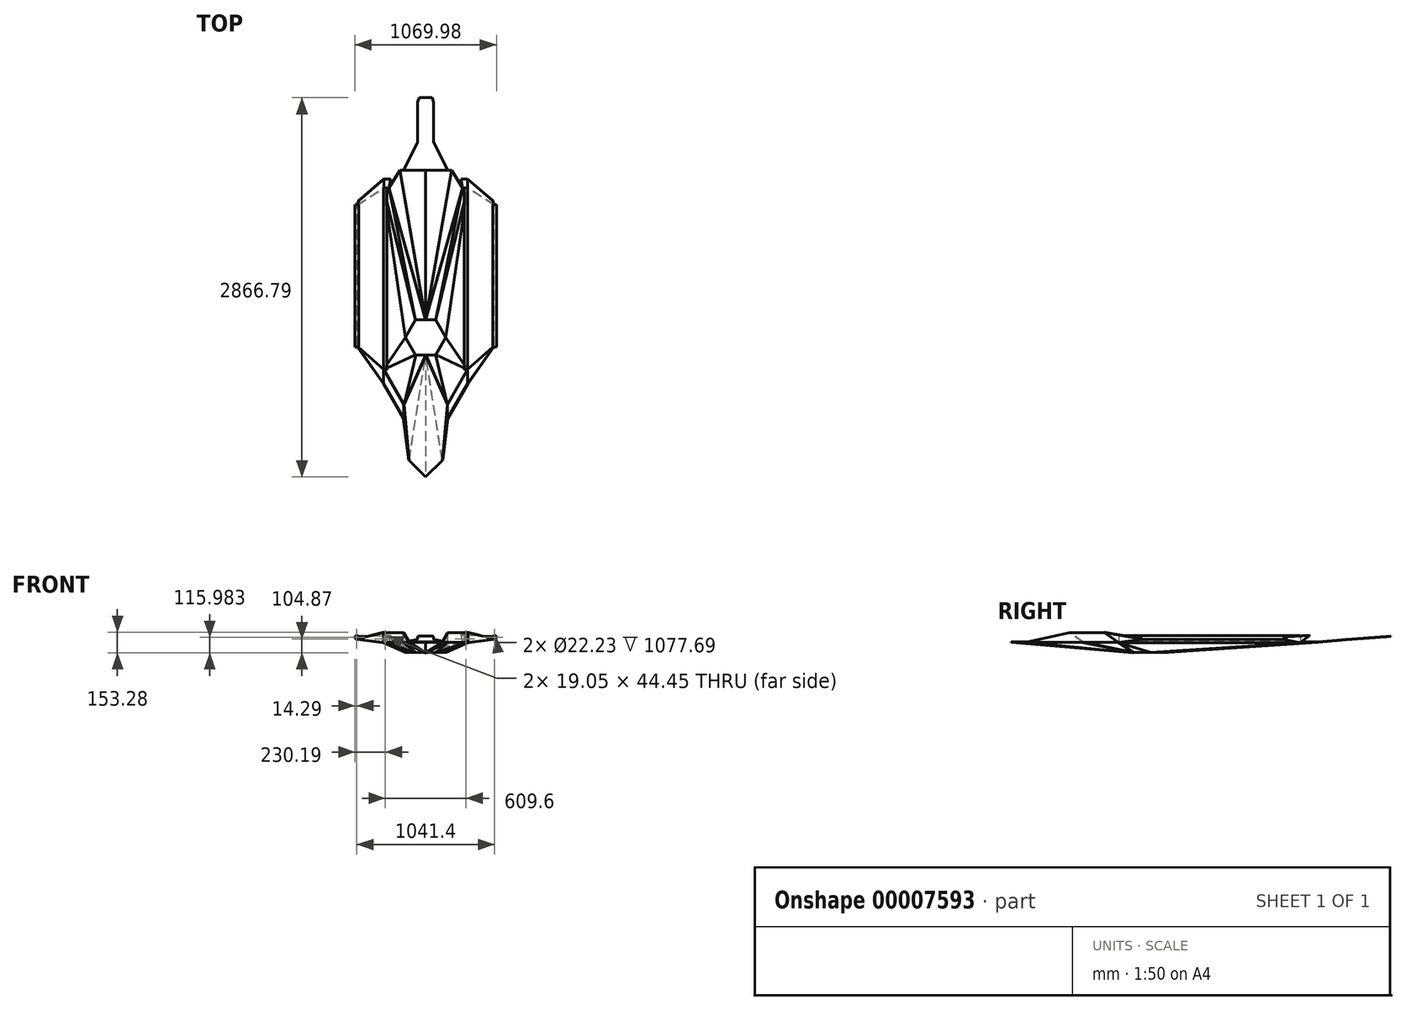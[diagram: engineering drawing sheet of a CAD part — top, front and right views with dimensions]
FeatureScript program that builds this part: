
annotation { "Feature Type Name" : "Feature", "Feature Type Description" : "" }
export const myFeature = defineFeature(function(context is Context, id is Id, definition is map)
    precondition{}
    {
        {
            var Q0;
            Q0=qCreatedBy(makeId("Top.planeOp"),FACE);
            var sketch = newSketch(context, id + "F0", { "sketchPlane" : qUnion([Q0])});
            skLineSegment(sketch, "E0.bottom", {"start": v(-317.5, -685.8) * mm, "end": v(317.5, -685.8) * mm});
            skLineSegment(sketch, "E0.top", {"start": v(-317.5, 685.8) * mm, "end": v(317.5, 685.8) * mm});
            skLineSegment(sketch, "E0.left", {"start": v(-317.5, -685.8) * mm, "end": v(-317.5, 685.8) * mm});
            skLineSegment(sketch, "E0.right", {"start": v(317.5, -685.8) * mm, "end": v(317.5, 685.8) * mm});
            skPoint(sketch, "E0.middle", {"position": v(0, 0) * mm});
            skLineSegment(sketch, "E1", {"start": v(0, -1498.6) * mm, "end": v(0, 1371.6) * mm, "construction": true});
            skLineSegment(sketch, "E2.0", {"start": v(-520.7, -508) * mm, "end": v(-520.7, 558.8) * mm});
            skLineSegment(sketch, "E3.0", {"start": v(520.7, -508) * mm, "end": v(520.7, 558.8) * mm});
            skLineSegment(sketch, "E4", {"start": v(317.5, -685.8) * mm, "end": v(520.7, -508) * mm});
            skLineSegment(sketch, "E5", {"start": v(520.7, 558.8) * mm, "end": v(317.5, 685.8) * mm});
            skLineSegment(sketch, "E6.MirrorCS", {"start": v(-520.7, 558.8) * mm, "end": v(-317.5, 685.8) * mm});
            skLineSegment(sketch, "E7.MirrorCS", {"start": v(-317.5, -685.8) * mm, "end": v(-520.7, -508) * mm});
            skLineSegment(sketch, "E8", {"start": v(278.86, 685.8) * mm, "end": v(195.2, 819.67) * mm});
            skLineSegment(sketch, "E9", {"start": v(195.2, 819.67) * mm, "end": v(167.22, 819.67) * mm});
            skLineSegment(sketch, "E10.MirrorCS", {"start": v(-195.2, 819.67) * mm, "end": v(-167.22, 819.67) * mm});
            skLineSegment(sketch, "E11.MirrorCS", {"start": v(-278.86, 685.8) * mm, "end": v(-195.2, 819.67) * mm});
            skLineSegment(sketch, "E12", {"start": v(317.5, -685.8) * mm, "end": v(164.9, -952) * mm});
            skLineSegment(sketch, "E13", {"start": v(164.9, -952) * mm, "end": v(125.97, -1373.7) * mm});
            skLineSegment(sketch, "E14", {"start": v(125.97, -1373.7) * mm, "end": v(0, -1498.6) * mm});
            skLineSegment(sketch, "E15.MirrorCS", {"start": v(-164.9, -952) * mm, "end": v(-125.97, -1373.7) * mm});
            skLineSegment(sketch, "E16.MirrorCS", {"start": v(-317.5, -685.8) * mm, "end": v(-164.9, -952) * mm});
            skLineSegment(sketch, "E17.MirrorCS", {"start": v(-125.97, -1373.7) * mm, "end": v(0, -1498.6) * mm});
            skLineSegment(sketch, "E18", {"start": v(167.22, 819.67) * mm, "end": v(60.58, 1033.46) * mm});
            skLineSegment(sketch, "E19", {"start": v(60.58, 1033.46) * mm, "end": v(60.58, 1338.26) * mm});
            skLineSegment(sketch, "E20", {"start": v(60.58, 1338.26) * mm, "end": v(50.3, 1371.6) * mm});
            skLineSegment(sketch, "E21", {"start": v(50.3, 1371.6) * mm, "end": v(0, 1371.6) * mm});
            skLineSegment(sketch, "E22.MirrorCS", {"start": v(-50.3, 1371.6) * mm, "end": v(0, 1371.6) * mm});
            skLineSegment(sketch, "E23.MirrorCS", {"start": v(-60.58, 1338.26) * mm, "end": v(-50.3, 1371.6) * mm});
            skLineSegment(sketch, "E24.MirrorCS", {"start": v(-60.58, 1033.46) * mm, "end": v(-60.58, 1338.26) * mm});
            skLineSegment(sketch, "E25.MirrorCS", {"start": v(-167.22, 819.67) * mm, "end": v(-60.58, 1033.46) * mm});
            skPoint(sketch, "E26.orphan", {"position": v(0, 819.67) * mm});
            skSolve(sketch);
        }
        {
            var Q0;
            Q0=qCreatedBy(makeId("Top.planeOp"),FACE);
            cPlane(context, id + "F1", {"entities" : qUnion([Q0]), "cplaneType" : CPlaneType.OFFSET, "offset" : 76.2 * mm, "oppositeDirection" : true, "width" : 152.4 * mm, "height" : 152.4 * mm});
        }
        {
            var Q0;
            Q0=qCreatedBy(id+"F1.planeOp",FACE);
            var sketch = newSketch(context, id + "F2", { "sketchPlane" : qUnion([Q0])});
            skCircle(sketch, "E27.cCircle", {"center": v(0, -443.6) * mm, "radius": 131.98 * mm, "construction": true});
            skLineSegment(sketch, "E27.0", {"start": v(76.2, -575.58) * mm, "end": v(-76.2, -575.58) * mm});
            skLineSegment(sketch, "E27.1", {"start": v(-76.2, -575.58) * mm, "end": v(-152.4, -443.6) * mm});
            skLineSegment(sketch, "E27.2", {"start": v(-152.4, -443.6) * mm, "end": v(-76.2, -311.61) * mm});
            skLineSegment(sketch, "E27.3", {"start": v(-76.2, -311.61) * mm, "end": v(76.2, -311.61) * mm});
            skLineSegment(sketch, "E27.4", {"start": v(76.2, -311.61) * mm, "end": v(152.4, -443.6) * mm});
            skLineSegment(sketch, "E27.5", {"start": v(152.4, -443.6) * mm, "end": v(76.2, -575.58) * mm});
            skPoint(sketch, "E27.0.midPoint", {"position": v(0, -575.58) * mm});
            skPoint(sketch, "E28", {"position": v(0, -311.61) * mm});
            skSolve(sketch);
        }
        {
            var Q0;
            Q0 = qSketchRegion(id + "F2", true);
            extrude(context, id + "F3", {"entities" : qUnion([Q0]), "depth" : 3.33 * mm});
        }
        {
            var Q0;
            Q0=makeQuery(id+"F3.opExtrude","CAP_VERTEX",VERTEX,{"disambiguationData":[OSD([sQuery(id+"F2.wireOp",EDGE,"E27.1"),sQuery(id+"F2.wireOp",EDGE,"E27.2")])],"isStart":false});
            var Q1;
            Q1=makeQuery(id+"F3.opExtrude","CAP_VERTEX",VERTEX,{"disambiguationData":[OSD([sQuery(id+"F2.wireOp",EDGE,"E27.2"),sQuery(id+"F2.wireOp",EDGE,"E27.3")])],"isStart":false});
            var Q2;
            Q2=sQuery(id+"F0.wireOp",VERTEX,"E0.left.end");
            cPlane(context, id + "F4", {"entities" : qUnion([Q0, Q1, Q2]), "cplaneType" : CPlaneType.THREE_POINT, "offset" : 152.4 * mm, "width" : 152.4 * mm, "height" : 152.4 * mm});
        }
        {
            var Q0;
            Q0=qCreatedBy(id+"F4.planeOp",FACE);
            var sketch = newSketch(context, id + "F5", { "sketchPlane" : qUnion([Q0])});
            skPoint(sketch, "E29.0", {"position": v(-147.37, 446.76) * mm});
            skPoint(sketch, "E29.1", {"position": v(-70.87, 314.95) * mm});
            skPoint(sketch, "E29.2", {"position": v(-313.12, -684.9) * mm});
            skLineSegment(sketch, "E30", {"start": v(-313.12, -684.9) * mm, "end": v(-70.87, 314.95) * mm});
            skLineSegment(sketch, "E31", {"start": v(-147.37, 446.76) * mm, "end": v(-313.12, -684.9) * mm});
            skLineSegment(sketch, "E32", {"start": v(-147.37, 446.76) * mm, "end": v(-70.87, 314.95) * mm});
            skSolve(sketch);
        }
        {
            var Q0;
            Q0 = qSketchRegion(id + "F5", true);
            extrude(context, id + "F6", {"entities" : qUnion([Q0]), "depth" : 3.33 * mm});
        }
        {
            var Q0;
            Q0=qCreatedBy(makeId("Top.planeOp"),FACE);
            var sketch = newSketch(context, id + "F7", { "sketchPlane" : qUnion([Q0])});
            skPoint(sketch, "E33.0", {"position": v(317.5, 685.8) * mm});
            skPoint(sketch, "E33.1", {"position": v(317.5, -685.8) * mm});
            skLineSegment(sketch, "E34.bottom", {"start": v(317.5, -685.8) * mm, "end": v(292.1, -685.8) * mm});
            skLineSegment(sketch, "E34.top", {"start": v(317.5, 685.8) * mm, "end": v(292.1, 685.8) * mm});
            skLineSegment(sketch, "E34.left", {"start": v(317.5, -685.8) * mm, "end": v(317.5, 685.8) * mm});
            skLineSegment(sketch, "E34.right", {"start": v(292.1, -685.8) * mm, "end": v(292.1, 685.8) * mm});
            skSolve(sketch);
        }
        {
            var Q0;
            Q0=sQuery(id+"F7.wireOp",EDGE,"E34.bottom");
            cPlane(context, id + "F8", {"entities" : qUnion([Q0]), "cplaneType" : CPlaneType.LINE_ANGLE, "offset" : 152.4 * mm, "angle" : 0 * degree, "width" : 152.4 * mm, "height" : 152.4 * mm});
        }
        {
            var Q0;
            Q0=qCreatedBy(id+"F8.planeOp",FACE);
            var sketch = newSketch(context, id + "F9", { "sketchPlane" : qUnion([Q0])});
            skLineSegment(sketch, "E35.bottom", {"start": v(295.28, 50.8) * mm, "end": v(314.33, 50.8) * mm});
            skLineSegment(sketch, "E35.top", {"start": v(295.28, 0) * mm, "end": v(314.33, 0) * mm});
            skLineSegment(sketch, "E35.left", {"start": v(292.1, 47.62) * mm, "end": v(292.1, 3.18) * mm});
            skLineSegment(sketch, "E35.right", {"start": v(317.5, 47.62) * mm, "end": v(317.5, 3.18) * mm});
            skPoint(sketch, "E36.visualSharp", {"position": v(317.5, 0) * mm});
            skArc(sketch, "E36.filletArc", {"start": v(314.33, 0) * mm, "mid": v(316.57, 0.93) * mm, "end": v(317.5, 3.18) * mm});
            skPoint(sketch, "E37.visualSharp", {"position": v(292.1, 0) * mm});
            skArc(sketch, "E37.filletArc", {"start": v(292.1, 3.18) * mm, "mid": v(293.03, 0.93) * mm, "end": v(295.28, 0) * mm});
            skPoint(sketch, "E38.visualSharp", {"position": v(292.1, 50.8) * mm});
            skArc(sketch, "E38.filletArc", {"start": v(295.28, 50.8) * mm, "mid": v(293.03, 49.87) * mm, "end": v(292.1, 47.62) * mm});
            skPoint(sketch, "E39.visualSharp", {"position": v(317.5, 50.8) * mm});
            skArc(sketch, "E39.filletArc", {"start": v(317.5, 47.62) * mm, "mid": v(316.57, 49.87) * mm, "end": v(314.33, 50.8) * mm});
            skLineSegment(sketch, "E40.0", {"start": v(295.28, 47.62) * mm, "end": v(314.33, 47.62) * mm});
            skLineSegment(sketch, "E40.1", {"start": v(295.28, 47.62) * mm, "end": v(295.28, 3.17) * mm});
            skLineSegment(sketch, "E40.2", {"start": v(295.28, 3.17) * mm, "end": v(314.33, 3.17) * mm});
            skLineSegment(sketch, "E40.3", {"start": v(314.33, 47.62) * mm, "end": v(314.33, 3.17) * mm});
            skSolve(sketch);
        }
        {
            var Q0;
            Q0 = qSketchRegion(id + "F9", true);
            extrude(context, id + "F10", {"entities" : qUnion([Q0]), "oppositeDirection" : true, "depth" : 1371.6 * mm});
        }
        {
            var Q0;
            Q0=makeQuery(id+"F10.opExtrude","SWEPT_BODY",BODY,{"disambiguationData":[OSD([sQuery(id+"F9.wireOp",EDGE,"E35.bottom"),sQuery(id+"F9.wireOp",EDGE,"E35.top"),sQuery(id+"F9.wireOp",EDGE,"E35.left"),sQuery(id+"F9.wireOp",EDGE,"E35.right"),sQuery(id+"F9.wireOp",EDGE,"E36.filletArc"),sQuery(id+"F9.wireOp",EDGE,"E37.filletArc"),sQuery(id+"F9.wireOp",EDGE,"E38.filletArc"),sQuery(id+"F9.wireOp",EDGE,"E39.filletArc"),sQuery(id+"F9.wireOp",EDGE,"E40.0"),sQuery(id+"F9.wireOp",EDGE,"E40.1"),sQuery(id+"F9.wireOp",EDGE,"E40.2"),sQuery(id+"F9.wireOp",EDGE,"E40.3")])]});
            var Q1;
            Q1=qCreatedBy(makeId("Right.planeOp"),FACE);
            mirror(context, id + "F11", {"entities" : qUnion([Q0]), "mirrorPlane" : qUnion([Q1])});
        }
        {
            var Q0;
            Q0=makeQuery(id+"F6.opExtrude","SWEPT_BODY",BODY,{"disambiguationData":[OSD([sQuery(id+"F5.wireOp",EDGE,"E30"),sQuery(id+"F5.wireOp",EDGE,"E31"),sQuery(id+"F5.wireOp",EDGE,"E32")])]});
            var Q1;
            Q1=qCreatedBy(makeId("Right.planeOp"),FACE);
            mirror(context, id + "F12", {"entities" : qUnion([Q0]), "mirrorPlane" : qUnion([Q1])});
        }
        {
            var Q0;
            Q0=makeQuery(id+"F12.opPattern","COPY",VERTEX,{"derivedFrom":makeQuery(id+"F6.opExtrude","CAP_VERTEX",VERTEX,{"disambiguationData":[OSD([sQuery(id+"F5.wireOp",EDGE,"E31"),sQuery(id+"F5.wireOp",EDGE,"E32")])],"isStart":true}),"instanceName":"1"});
            var Q1;
            Q1=makeQuery(id+"F3.opExtrude","CAP_VERTEX",VERTEX,{"disambiguationData":[OSD([sQuery(id+"F2.wireOp",EDGE,"E27.0"),sQuery(id+"F2.wireOp",EDGE,"E27.5")])],"isStart":false});
            var Q2;
            Q2=sQuery(id+"F7.wireOp",VERTEX,"E33.1");
            cPlane(context, id + "F13", {"entities" : qUnion([Q0, Q1, Q2]), "cplaneType" : CPlaneType.THREE_POINT, "offset" : 152.4 * mm, "width" : 152.4 * mm, "height" : 152.4 * mm});
        }
        {
            var Q0;
            Q0=qCreatedBy(id+"F13.planeOp",FACE);
            var sketch = newSketch(context, id + "F14", { "sketchPlane" : qUnion([Q0])});
            skPoint(sketch, "E41.0", {"position": v(38.64, 559.76) * mm});
            skPoint(sketch, "E41.1", {"position": v(116.94, 429.02) * mm});
            skPoint(sketch, "E41.2", {"position": v(287.37, 679.36) * mm});
            skLineSegment(sketch, "E42", {"start": v(116.94, 429.02) * mm, "end": v(287.37, 679.36) * mm});
            skLineSegment(sketch, "E43", {"start": v(116.94, 429.02) * mm, "end": v(38.64, 559.76) * mm});
            skLineSegment(sketch, "E44", {"start": v(38.64, 559.76) * mm, "end": v(287.37, 679.36) * mm});
            skSolve(sketch);
        }
        {
            var Q0;
            Q0 = qSketchRegion(id + "F14", true);
            extrude(context, id + "F15", {"entities" : qUnion([Q0]), "depth" : 3.33 * mm});
        }
        {
            var Q0;
            Q0=makeQuery(id+"F15.opExtrude","SWEPT_BODY",BODY,{"disambiguationData":[OSD([sQuery(id+"F14.wireOp",EDGE,"E42"),sQuery(id+"F14.wireOp",EDGE,"E43"),sQuery(id+"F14.wireOp",EDGE,"E44")])]});
            var Q1;
            Q1=qCreatedBy(makeId("Right.planeOp"),FACE);
            mirror(context, id + "F16", {"operationType" : NewBodyOperationType.ADD, "entities" : qUnion([Q0]), "mirrorPlane" : qUnion([Q1])});
        }
        {
            var Q0;
            Q0=sQuery(id+"F5.wireOp",VERTEX,"E29.0");
            var Q1;
            Q1=makeQuery(id+"F16.opPattern","COPY",VERTEX,{"derivedFrom":makeQuery(id+"F15.opExtrude","CAP_VERTEX",VERTEX,{"disambiguationData":[OSD([sQuery(id+"F14.wireOp",EDGE,"E42"),sQuery(id+"F14.wireOp",EDGE,"E44")])],"isStart":true}),"instanceName":"1"});
            var Q2;
            Q2=sQuery(id+"F5.wireOp",VERTEX,"E29.2");
            cPlane(context, id + "F17", {"entities" : qUnion([Q0, Q1, Q2]), "cplaneType" : CPlaneType.THREE_POINT, "offset" : 152.4 * mm, "width" : 152.4 * mm, "height" : 152.4 * mm});
        }
        {
            var Q0;
            Q0=qCreatedBy(id+"F17.planeOp",FACE);
            var sketch = newSketch(context, id + "F18", { "sketchPlane" : qUnion([Q0])});
            skPoint(sketch, "E45.0", {"position": v(-110, -443.6) * mm});
            skPoint(sketch, "E45.1", {"position": v(-290.46, -685.8) * mm});
            skPoint(sketch, "E45.2", {"position": v(-290.46, 685.8) * mm});
            skLineSegment(sketch, "E46", {"start": v(-290.46, -685.8) * mm, "end": v(-110, -443.6) * mm});
            skLineSegment(sketch, "E47", {"start": v(-290.46, 685.8) * mm, "end": v(-290.46, -685.8) * mm});
            skLineSegment(sketch, "E48", {"start": v(-110, -443.6) * mm, "end": v(-290.46, 685.8) * mm});
            skSolve(sketch);
        }
        {
            var Q0;
            Q0 = qSketchRegion(id + "F18", true);
            extrude(context, id + "F19", {"entities" : qUnion([Q0]), "oppositeDirection" : true, "depth" : 3.33 * mm});
        }
        {
            var Q0;
            Q0=makeQuery(id+"F19.opExtrude","SWEPT_BODY",BODY,{"disambiguationData":[OSD([sQuery(id+"F18.wireOp",EDGE,"E46"),sQuery(id+"F18.wireOp",EDGE,"E47"),sQuery(id+"F18.wireOp",EDGE,"E48")])]});
            var Q1;
            Q1=qCreatedBy(makeId("Right.planeOp"),FACE);
            mirror(context, id + "F20", {"operationType" : NewBodyOperationType.ADD, "entities" : qUnion([Q0]), "mirrorPlane" : qUnion([Q1])});
        }
        {
            var Q0;
            Q0=sQuery(id+"F2.wireOp",VERTEX,"E27.0.midPoint");
            var Q1;
            Q1=sQuery(id+"F14.wireOp",VERTEX,"E41.0");
            var Q2;
            Q2=sQuery(id+"F0.wireOp",VERTEX,"E13.start");
            cPlane(context, id + "F21", {"entities" : qUnion([Q0, Q1, Q2]), "cplaneType" : CPlaneType.THREE_POINT, "offset" : 152.4 * mm, "width" : 152.4 * mm, "height" : 152.4 * mm});
        }
        {
            var Q0;
            Q0=qCreatedBy(id+"F21.planeOp",FACE);
            var sketch = newSketch(context, id + "F22", { "sketchPlane" : qUnion([Q0])});
            skPoint(sketch, "E49.0", {"position": v(-7.4, -552.28) * mm});
            skPoint(sketch, "E49.1", {"position": v(68.74, -552.28) * mm});
            skPoint(sketch, "E49.2", {"position": v(157.64, -936.27) * mm});
            skLineSegment(sketch, "E50", {"start": v(-7.4, -552.28) * mm, "end": v(68.74, -552.28) * mm});
            skLineSegment(sketch, "E51", {"start": v(-7.4, -552.28) * mm, "end": v(157.64, -936.27) * mm});
            skLineSegment(sketch, "E52", {"start": v(68.74, -552.28) * mm, "end": v(157.64, -936.27) * mm});
            skSolve(sketch);
        }
        {
            var Q0;
            Q0 = qSketchRegion(id + "F22", true);
            extrude(context, id + "F23", {"entities" : qUnion([Q0]), "oppositeDirection" : true, "depth" : 3.33 * mm});
        }
        {
            var Q0;
            Q0=sQuery(id+"F2.wireOp",VERTEX,"E27.5.end");
            var Q1;
            Q1=sQuery(id+"F0.wireOp",VERTEX,"E13.start");
            var Q2;
            Q2=sQuery(id+"F14.wireOp",VERTEX,"E41.2");
            cPlane(context, id + "F24", {"entities" : qUnion([Q0, Q1, Q2]), "cplaneType" : CPlaneType.THREE_POINT, "offset" : 152.4 * mm, "width" : 152.4 * mm, "height" : 152.4 * mm});
        }
        {
            var Q0;
            Q0=qCreatedBy(id+"F24.planeOp",FACE);
            var sketch = newSketch(context, id + "F25", { "sketchPlane" : qUnion([Q0])});
            skPoint(sketch, "E53.0", {"position": v(127.55, 942.35) * mm});
            skPoint(sketch, "E53.1", {"position": v(284.77, 678.85) * mm});
            skLineSegment(sketch, "E54", {"start": v(36.17, 558.92) * mm, "end": v(127.55, 942.35) * mm});
            skLineSegment(sketch, "E55", {"start": v(284.77, 678.85) * mm, "end": v(127.55, 942.35) * mm});
            skLineSegment(sketch, "E56", {"start": v(36.17, 558.92) * mm, "end": v(284.77, 678.85) * mm});
            skPoint(sketch, "E57.0", {"position": v(36.17, 558.92) * mm});
            skSolve(sketch);
        }
        {
            var Q0;
            Q0 = qSketchRegion(id + "F25", true);
            extrude(context, id + "F26", {"entities" : qUnion([Q0]), "oppositeDirection" : true, "depth" : 3.33 * mm});
        }
        {
            var Q0;
            Q0=makeQuery(id+"F26.opExtrude","SWEPT_BODY",BODY,{"disambiguationData":[OSD([sQuery(id+"F25.wireOp",EDGE,"E54"),sQuery(id+"F25.wireOp",EDGE,"E55"),sQuery(id+"F25.wireOp",EDGE,"E56")])]});
            var Q1;
            Q1=makeQuery(id+"F23.opExtrude","SWEPT_BODY",BODY,{"disambiguationData":[OSD([sQuery(id+"F22.wireOp",EDGE,"E50"),sQuery(id+"F22.wireOp",EDGE,"E51"),sQuery(id+"F22.wireOp",EDGE,"E52")])]});
            var Q2;
            Q2=qCreatedBy(makeId("Right.planeOp"),FACE);
            mirror(context, id + "F27", {"entities" : qUnion([Q0, Q1]), "mirrorPlane" : qUnion([Q2])});
        }
        {
            var Q0;
            Q0=sQuery(id+"F2.wireOp",VERTEX,"E28");
            var Q1;
            Q1=sQuery(id+"F2.wireOp",VERTEX,"E27.4.start");
            var Q2;
            Q2=sQuery(id+"F0.wireOp",VERTEX,"E8.start");
            cPlane(context, id + "F28", {"entities" : qUnion([Q0, Q1, Q2]), "cplaneType" : CPlaneType.THREE_POINT, "offset" : 152.4 * mm, "width" : 152.4 * mm, "height" : 152.4 * mm});
        }
        {
            var Q0;
            Q0=qCreatedBy(id+"F28.planeOp",FACE);
            var sketch = newSketch(context, id + "F29", { "sketchPlane" : qUnion([Q0])});
            skPoint(sketch, "E58.0", {"position": v(278.86, -683.8) * mm});
            skPoint(sketch, "E58.1", {"position": v(76.2, 316.51) * mm});
            skPoint(sketch, "E58.2", {"position": v(0, 316.51) * mm});
            skLineSegment(sketch, "E59", {"start": v(278.86, -683.8) * mm, "end": v(76.2, 316.51) * mm});
            skLineSegment(sketch, "E60", {"start": v(0, 316.51) * mm, "end": v(76.2, 316.51) * mm});
            skLineSegment(sketch, "E61", {"start": v(0, 316.51) * mm, "end": v(278.86, -683.8) * mm});
            skSolve(sketch);
        }
        {
            var Q0;
            Q0 = qSketchRegion(id + "F29", true);
            extrude(context, id + "F30", {"entities" : qUnion([Q0]), "oppositeDirection" : true, "depth" : 3.33 * mm});
        }
        {
            var Q0;
            Q0=makeQuery(id+"F30.opExtrude","SWEPT_BODY",BODY,{"disambiguationData":[OSD([sQuery(id+"F29.wireOp",EDGE,"E59"),sQuery(id+"F29.wireOp",EDGE,"E60"),sQuery(id+"F29.wireOp",EDGE,"E61")])]});
            var Q1;
            Q1=qCreatedBy(makeId("Right.planeOp"),FACE);
            mirror(context, id + "F31", {"entities" : qUnion([Q0]), "mirrorPlane" : qUnion([Q1])});
        }
        {
            var Q0;
            Q0=makeQuery(id+"F23.opExtrude","CAP_VERTEX",VERTEX,{"disambiguationData":[OSD([sQuery(id+"F22.wireOp",EDGE,"E50"),sQuery(id+"F22.wireOp",EDGE,"E51")])],"isStart":false});
            var Q1;
            Q1=sQuery(id+"F0.wireOp",VERTEX,"E14.start");
            var Q2;
            Q2=sQuery(id+"F0.wireOp",VERTEX,"E17.MirrorCS.end");
            cPlane(context, id + "F32", {"entities" : qUnion([Q0, Q1, Q2]), "cplaneType" : CPlaneType.THREE_POINT, "offset" : 152.4 * mm, "width" : 152.4 * mm, "height" : 152.4 * mm});
        }
        {
            var Q0;
            Q0=qCreatedBy(id+"F32.planeOp",FACE);
            var sketch = newSketch(context, id + "F33", { "sketchPlane" : qUnion([Q0])});
            skPoint(sketch, "E62.0", {"position": v(-10.77, -567.23) * mm});
            skPoint(sketch, "E62.1", {"position": v(115.5, -1368.62) * mm});
            skPoint(sketch, "E62.2", {"position": v(-10.91, -1493.07) * mm});
            skLineSegment(sketch, "E63", {"start": v(-10.77, -567.23) * mm, "end": v(-10.91, -1493.07) * mm});
            skLineSegment(sketch, "E64", {"start": v(115.5, -1368.62) * mm, "end": v(-10.91, -1493.07) * mm});
            skLineSegment(sketch, "E65", {"start": v(115.5, -1368.62) * mm, "end": v(-10.77, -567.23) * mm});
            skSolve(sketch);
        }
        {
            var Q0;
            Q0 = qSketchRegion(id + "F33", true);
            extrude(context, id + "F34", {"entities" : qUnion([Q0]), "depth" : 3.33 * mm});
        }
        {
            var Q0;
            Q0=makeQuery(id+"F34.opExtrude","SWEPT_BODY",BODY,{"disambiguationData":[OSD([sQuery(id+"F33.wireOp",EDGE,"E63"),sQuery(id+"F33.wireOp",EDGE,"E64"),sQuery(id+"F33.wireOp",EDGE,"E65")])]});
            var Q1;
            Q1=qCreatedBy(makeId("Right.planeOp"),FACE);
            mirror(context, id + "F35", {"entities" : qUnion([Q0]), "mirrorPlane" : qUnion([Q1])});
        }
        {
            var Q0;
            Q0=makeQuery(id+"F23.opExtrude","CAP_VERTEX",VERTEX,{"disambiguationData":[OSD([sQuery(id+"F22.wireOp",EDGE,"E50"),sQuery(id+"F22.wireOp",EDGE,"E51")])],"isStart":false});
            var Q1;
            Q1=makeQuery(id+"F23.opExtrude","CAP_VERTEX",VERTEX,{"disambiguationData":[OSD([sQuery(id+"F22.wireOp",EDGE,"E51"),sQuery(id+"F22.wireOp",EDGE,"E52")])],"isStart":false});
            var Q2;
            Q2=sQuery(id+"F0.wireOp",VERTEX,"E14.start");
            cPlane(context, id + "F36", {"entities" : qUnion([Q0, Q1, Q2]), "cplaneType" : CPlaneType.THREE_POINT, "offset" : 152.4 * mm, "width" : 152.4 * mm, "height" : 152.4 * mm});
        }
        {
            var Q0;
            Q0=qCreatedBy(id+"F36.planeOp",FACE);
            var sketch = newSketch(context, id + "F37", { "sketchPlane" : qUnion([Q0])});
            skPoint(sketch, "E66.0", {"position": v(98.55, -1372.5) * mm});
            skPoint(sketch, "E66.1", {"position": v(140.15, -951.63) * mm});
            skPoint(sketch, "E66.2", {"position": v(-35.46, -572.36) * mm});
            skLineSegment(sketch, "E67", {"start": v(-35.46, -572.36) * mm, "end": v(140.15, -951.63) * mm});
            skLineSegment(sketch, "E68", {"start": v(98.55, -1372.5) * mm, "end": v(140.15, -951.63) * mm});
            skLineSegment(sketch, "E69", {"start": v(98.55, -1372.5) * mm, "end": v(-35.46, -572.36) * mm});
            skSolve(sketch);
        }
        {
            var Q0;
            Q0 = qSketchRegion(id + "F37", true);
            extrude(context, id + "F38", {"entities" : qUnion([Q0]), "depth" : 3.33 * mm});
        }
        {
            var Q0;
            Q0=makeQuery(id+"F38.opExtrude","SWEPT_BODY",BODY,{"disambiguationData":[OSD([sQuery(id+"F37.wireOp",EDGE,"E67"),sQuery(id+"F37.wireOp",EDGE,"E68"),sQuery(id+"F37.wireOp",EDGE,"E69")])]});
            var Q1;
            Q1=qCreatedBy(makeId("Right.planeOp"),FACE);
            mirror(context, id + "F39", {"entities" : qUnion([Q0]), "mirrorPlane" : qUnion([Q1])});
        }
        {
            var Q0;
            Q0=sQuery(id+"F0.wireOp",VERTEX,"E8.end");
            var Q1;
            Q1=sQuery(id+"F29.wireOp",VERTEX,"E58.0");
            var Q2;
            Q2=sQuery(id+"F29.wireOp",VERTEX,"E58.2");
            cPlane(context, id + "F40", {"entities" : qUnion([Q0, Q1, Q2]), "cplaneType" : CPlaneType.THREE_POINT, "offset" : 152.4 * mm, "width" : 152.4 * mm, "height" : 152.4 * mm});
        }
        {
            var Q0;
            Q0=qCreatedBy(id+"F40.planeOp",FACE);
            var sketch = newSketch(context, id + "F41", { "sketchPlane" : qUnion([Q0])});
            skPoint(sketch, "E70.0", {"position": v(190.87, 818.53) * mm});
            skPoint(sketch, "E70.1", {"position": v(274.84, 684.85) * mm});
            skPoint(sketch, "E70.2", {"position": v(-5.01, -315.2) * mm});
            skLineSegment(sketch, "E71", {"start": v(190.87, 818.53) * mm, "end": v(274.84, 684.85) * mm});
            skLineSegment(sketch, "E72", {"start": v(274.84, 684.85) * mm, "end": v(-5.01, -315.2) * mm});
            skLineSegment(sketch, "E73", {"start": v(-5.01, -315.2) * mm, "end": v(190.87, 818.53) * mm});
            skSolve(sketch);
        }
        {
            var Q0;
            Q0 = qSketchRegion(id + "F41", true);
            extrude(context, id + "F42", {"entities" : qUnion([Q0]), "depth" : 3.33 * mm});
        }
        {
            var Q0;
            Q0=sQuery(id+"F0.wireOp",VERTEX,"E8.end");
            var Q1;
            Q1=sQuery(id+"F0.wireOp",VERTEX,"E26.orphan");
            var Q2;
            Q2=sQuery(id+"F29.wireOp",VERTEX,"E58.2");
            cPlane(context, id + "F43", {"entities" : qUnion([Q0, Q1, Q2]), "cplaneType" : CPlaneType.THREE_POINT, "offset" : 152.4 * mm, "width" : 152.4 * mm, "height" : 152.4 * mm});
        }
        {
            var Q0;
            Q0=qCreatedBy(id+"F43.planeOp",FACE);
            var sketch = newSketch(context, id + "F44", { "sketchPlane" : qUnion([Q0])});
            skPoint(sketch, "E74.0", {"position": v(195.2, -817.82) * mm});
            skPoint(sketch, "E74.1", {"position": v(0, -817.82) * mm});
            skPoint(sketch, "E74.2", {"position": v(0, 316.03) * mm});
            skLineSegment(sketch, "E75", {"start": v(0, -817.82) * mm, "end": v(195.2, -817.82) * mm});
            skLineSegment(sketch, "E76", {"start": v(195.2, -817.82) * mm, "end": v(0, 316.03) * mm});
            skLineSegment(sketch, "E77", {"start": v(0, 316.03) * mm, "end": v(0, -817.82) * mm});
            skSolve(sketch);
        }
        {
            var Q0;
            Q0 = qSketchRegion(id + "F44", true);
            extrude(context, id + "F45", {"entities" : qUnion([Q0]), "oppositeDirection" : true, "depth" : 3.33 * mm});
        }
        {
            var Q0;
            Q0=sQuery(id+"F29.wireOp",VERTEX,"E58.0");
            var Q1;
            Q1=sQuery(id+"F7.wireOp",VERTEX,"E33.0");
            var Q2;
            Q2=sQuery(id+"F29.wireOp",VERTEX,"E58.1");
            cPlane(context, id + "F46", {"entities" : qUnion([Q0, Q1, Q2]), "cplaneType" : CPlaneType.THREE_POINT, "offset" : 152.4 * mm, "width" : 152.4 * mm, "height" : 152.4 * mm});
        }
        {
            var Q0;
            Q0=qCreatedBy(id+"F46.planeOp",FACE);
            var sketch = newSketch(context, id + "F47", { "sketchPlane" : qUnion([Q0])});
            skPoint(sketch, "E78.0", {"position": v(278.86, 683.8) * mm});
            skPoint(sketch, "E78.1", {"position": v(317.5, 683.8) * mm});
            skPoint(sketch, "E78.2", {"position": v(76.2, -316.51) * mm});
            skLineSegment(sketch, "E79", {"start": v(76.2, -316.51) * mm, "end": v(317.5, 683.8) * mm});
            skLineSegment(sketch, "E80", {"start": v(317.5, 683.8) * mm, "end": v(278.86, 683.8) * mm});
            skLineSegment(sketch, "E81", {"start": v(278.86, 683.8) * mm, "end": v(76.2, -316.51) * mm});
            skSolve(sketch);
        }
        {
            var Q0;
            Q0 = qSketchRegion(id + "F47", true);
            extrude(context, id + "F48", {"entities" : qUnion([Q0]), "depth" : 3.33 * mm});
        }
        {
            var Q0;
            Q0=makeQuery(id+"F45.opExtrude","SWEPT_BODY",BODY,{"disambiguationData":[OSD([sQuery(id+"F44.wireOp",EDGE,"E75"),sQuery(id+"F44.wireOp",EDGE,"E76"),sQuery(id+"F44.wireOp",EDGE,"E77")])]});
            var Q1;
            Q1=makeQuery(id+"F42.opExtrude","SWEPT_BODY",BODY,{"disambiguationData":[OSD([sQuery(id+"F41.wireOp",EDGE,"E71"),sQuery(id+"F41.wireOp",EDGE,"E72"),sQuery(id+"F41.wireOp",EDGE,"E73")])]});
            var Q2;
            Q2=makeQuery(id+"F48.opExtrude","SWEPT_BODY",BODY,{"disambiguationData":[OSD([sQuery(id+"F47.wireOp",EDGE,"E79"),sQuery(id+"F47.wireOp",EDGE,"E80"),sQuery(id+"F47.wireOp",EDGE,"E81")])]});
            var Q3;
            Q3=qCreatedBy(makeId("Right.planeOp"),FACE);
            mirror(context, id + "F49", {"entities" : qUnion([Q0, Q1, Q2]), "mirrorPlane" : qUnion([Q3])});
        }
        {
            var Q0;
            Q0=qCreatedBy(makeId("Front.planeOp"),FACE);
            var sketch = newSketch(context, id + "F50", { "sketchPlane" : qUnion([Q0])});
            skPoint(sketch, "E82.0", {"position": v(317.5, 50.8) * mm});
            skPoint(sketch, "E83.0", {"position": v(520.7, 0) * mm});
            skPoint(sketch, "E84.0", {"position": v(317.5, 0) * mm});
            skLineSegment(sketch, "E85", {"start": v(317.5, 0) * mm, "end": v(520.7, 22.23) * mm});
            skCircle(sketch, "E86", {"center": v(520.7, 36.51) * mm, "radius": 14.29 * mm});
            skPoint(sketch, "E87", {"position": v(520.7, 50.8) * mm});
            skCircle(sketch, "E88.0", {"center": v(520.7, 36.51) * mm, "radius": 11.11 * mm});
            skSolve(sketch);
        }
        {
            var Q0;
            Q0 = qSketchRegion(id + "F50", true);
            extrude(context, id + "F51", {"entities" : qUnion([Q0]), "depth" : 516.5 * mm, "hasSecondDirection" : true, "secondDirectionOppositeDirection" : true, "secondDirectionDepth" : 561.2 * mm});
        }
        {
            var Q0;
            Q0=makeQuery(id+"F20.opPattern","COPY",VERTEX,{"derivedFrom":makeQuery(id+"F19.opExtrude","CAP_VERTEX",VERTEX,{"disambiguationData":[OSD([sQuery(id+"F18.wireOp",EDGE,"E46"),sQuery(id+"F18.wireOp",EDGE,"E47")])],"isStart":false}),"instanceName":"1"});
            var Q1;
            Q1=makeQuery(id+"F20.opPattern","COPY",VERTEX,{"derivedFrom":makeQuery(id+"F19.opExtrude","CAP_VERTEX",VERTEX,{"disambiguationData":[OSD([sQuery(id+"F18.wireOp",EDGE,"E47"),sQuery(id+"F18.wireOp",EDGE,"E48")])],"isStart":false}),"instanceName":"1"});
            var Q2;
            Q2=sQuery(id+"F50.wireOp",VERTEX,"E85.end");
            cPlane(context, id + "F52", {"entities" : qUnion([Q0, Q1, Q2]), "cplaneType" : CPlaneType.THREE_POINT, "offset" : 152.4 * mm, "width" : 152.4 * mm, "height" : 152.4 * mm});
        }
        {
            var Q0;
            Q0=qCreatedBy(id+"F52.planeOp",FACE);
            var sketch = newSketch(context, id + "F53", { "sketchPlane" : qUnion([Q0])});
            skLineSegment(sketch, "E89.0", {"start": v(315.04, -685.8) * mm, "end": v(516.67, -508) * mm});
            skLineSegment(sketch, "E89.1", {"start": v(516.67, -508) * mm, "end": v(516.67, 558.8) * mm});
            skLineSegment(sketch, "E89.2", {"start": v(516.67, 558.8) * mm, "end": v(315.04, 685.8) * mm});
            skLineSegment(sketch, "E90", {"start": v(315.04, -685.8) * mm, "end": v(315.04, 685.8) * mm});
            skSolve(sketch);
        }
        {
            var Q0;
            Q0 = qSketchRegion(id + "F53", true);
            extrude(context, id + "F54", {"entities" : qUnion([Q0]), "depth" : 3.17 * mm});
        }
        {
            var Q0;
            Q0=makeQuery(id+"F54.opExtrude","SWEPT_BODY",BODY,{"disambiguationData":[OSD([sQuery(id+"F53.wireOp",EDGE,"E89.0"),sQuery(id+"F53.wireOp",EDGE,"E89.1"),sQuery(id+"F53.wireOp",EDGE,"E89.2"),sQuery(id+"F53.wireOp",EDGE,"E90")])]});
            var Q1;
            Q1=makeQuery(id+"F51.opExtrude","SWEPT_BODY",BODY,{"disambiguationData":[OSD([sQuery(id+"F50.wireOp",EDGE,"E86"),sQuery(id+"F50.wireOp",EDGE,"E88.0")])]});
            var Q2;
            Q2=qCreatedBy(makeId("Right.planeOp"),FACE);
            mirror(context, id + "F55", {"entities" : qUnion([Q0, Q1]), "mirrorPlane" : qUnion([Q2])});
        }
        {
            var Q0;
            Q0=makeQuery(id+"F45.opExtrude","CAP_EDGE",EDGE,{"disambiguationData":[OSD([sQuery(id+"F44.wireOp",EDGE,"E75")])],"isStart":false});
            var Q1;
            {var subQ1=sQuery(id+"F0.wireOp",EDGE,"E8");Q1=makeQuery(id+"F0.imprint","IMPRINT",FACE,{"disambiguationData":[TD([[makeQuery(id+"F0.imprint","IMPRINT",EDGE,{"derivedFrom":subQ1}),1.0]])]});}
            cPlane(context, id + "F56", {"entities" : qUnion([Q0, Q1]), "cplaneType" : CPlaneType.LINE_ANGLE, "offset" : 152.4 * mm, "angle" : 4.5 * degree, "width" : 152.4 * mm, "height" : 152.4 * mm});
        }
        {
            var Q0;
            Q0=qCreatedBy(id+"F56.planeOp",FACE);
            var sketch = newSketch(context, id + "F57", { "sketchPlane" : qUnion([Q0])});
            skLineSegment(sketch, "E91.0.4", {"start": v(167.22, -817.15) * mm, "end": v(60.58, -1030.27) * mm});
            skLineSegment(sketch, "E91.0.5", {"start": v(60.58, -1030.27) * mm, "end": v(60.58, -1334.13) * mm});
            skLineSegment(sketch, "E91.0.6", {"start": v(60.58, -1334.13) * mm, "end": v(50.3, -1367.37) * mm});
            skLineSegment(sketch, "E91.0.7", {"start": v(50.3, -1367.37) * mm, "end": v(0, -1367.37) * mm});
            skLineSegment(sketch, "E91.0.8", {"start": v(0, -1367.37) * mm, "end": v(-50.3, -1367.37) * mm});
            skLineSegment(sketch, "E91.0.9", {"start": v(-50.3, -1367.37) * mm, "end": v(-60.58, -1334.13) * mm});
            skLineSegment(sketch, "E91.0.10", {"start": v(-60.58, -1334.13) * mm, "end": v(-60.58, -1030.27) * mm});
            skLineSegment(sketch, "E91.0.11", {"start": v(-60.58, -1030.27) * mm, "end": v(-167.22, -817.15) * mm});
            skLineSegment(sketch, "E92", {"start": v(-167.22, -817.15) * mm, "end": v(167.22, -817.15) * mm});
            skSolve(sketch);
        }
        {
            var Q0;
            Q0 = qSketchRegion(id + "F57", true);
            extrude(context, id + "F58", {"entities" : qUnion([Q0]), "depth" : 3.17 * mm});
        }
        {
            var Q0;
            Q0=makeQuery(id+"F55.opPattern","COPY",EDGE,{"derivedFrom":makeQuery(id+"F54.opExtrude","CAP_EDGE",EDGE,{"disambiguationData":[OSD([sQuery(id+"F53.wireOp",EDGE,"E89.0")])],"isStart":false}),"instanceName":"1"});
            var Q1;
            Q1=qCreatedBy(makeId("Top.planeOp"),FACE);
            cPlane(context, id + "F59", {"entities" : qUnion([Q0, Q1]), "cplaneType" : CPlaneType.LINE_ANGLE, "offset" : 152.4 * mm, "angle" : 45 * degree, "width" : 152.4 * mm, "height" : 152.4 * mm});
        }
        {
            var Q0;
            Q0=qCreatedBy(id+"F59.planeOp",FACE);
            var sketch = newSketch(context, id + "F60", { "sketchPlane" : qUnion([Q0])});
            skPoint(sketch, "E93.0", {"position": v(-69.55, 564.84) * mm});
            skPoint(sketch, "E93.1", {"position": v(-303.6, 432.6) * mm});
            skLineSegment(sketch, "E94", {"start": v(-69.55, 564.84) * mm, "end": v(-303.6, 432.6) * mm});
            skLineSegment(sketch, "E95", {"start": v(-303.6, 432.6) * mm, "end": v(-69.55, 695) * mm});
            skLineSegment(sketch, "E96", {"start": v(-69.55, 695) * mm, "end": v(-69.55, 564.84) * mm});
            skSolve(sketch);
        }
        {
            var Q0;
            Q0 = qSketchRegion(id + "F60", true);
            extrude(context, id + "F61", {"entities" : qUnion([Q0]), "depth" : 3.17 * mm});
        }
        {
            var Q0;
            Q0=sQuery(id+"F0.wireOp",VERTEX,"E16.MirrorCS.end");
            var Q1;
            Q1=sQuery(id+"F60.wireOp",VERTEX,"E93.0");
            var Q2;
            Q2=sQuery(id+"F60.wireOp",VERTEX,"E95.end");
            cPlane(context, id + "F62", {"entities" : qUnion([Q0, Q1, Q2]), "cplaneType" : CPlaneType.THREE_POINT, "offset" : 152.4 * mm, "width" : 152.4 * mm, "height" : 152.4 * mm});
        }
        {
            var Q0;
            Q0=qCreatedBy(id+"F62.planeOp",FACE);
            var sketch = newSketch(context, id + "F63", { "sketchPlane" : qUnion([Q0])});
            skPoint(sketch, "E97.0", {"position": v(820.1, 105.5) * mm});
            skPoint(sketch, "E97.1", {"position": v(529.2, 203.16) * mm});
            skPoint(sketch, "E97.2", {"position": v(646.35, 259.88) * mm});
            skLineSegment(sketch, "E98", {"start": v(646.35, 259.88) * mm, "end": v(529.2, 203.16) * mm});
            skLineSegment(sketch, "E99", {"start": v(529.2, 203.16) * mm, "end": v(820.1, 105.5) * mm});
            skLineSegment(sketch, "E100", {"start": v(820.1, 105.5) * mm, "end": v(934.92, 161.11) * mm});
            skLineSegment(sketch, "E101", {"start": v(934.92, 161.11) * mm, "end": v(646.35, 259.88) * mm});
            skSolve(sketch);
        }
        {
            var Q0;
            Q0 = qSketchRegion(id + "F63", true);
            extrude(context, id + "F64", {"entities" : qUnion([Q0]), "operationType" : NewBodyOperationType.ADD, "depth" : 3.17 * mm});
        }
        {
            var Q0;
            Q0=makeQuery(id+"F39.opPattern","COPY",VERTEX,{"derivedFrom":makeQuery(id+"F38.opExtrude","CAP_VERTEX",VERTEX,{"disambiguationData":[OSD([sQuery(id+"F37.wireOp",EDGE,"E68"),sQuery(id+"F37.wireOp",EDGE,"E69")])],"isStart":false}),"instanceName":"1"});
            var Q1;
            Q1=sQuery(id+"F0.wireOp",VERTEX,"E16.MirrorCS.end");
            var Q2;
            Q2=makeQuery(id+"F64.opExtrude","CAP_VERTEX",VERTEX,{"disambiguationData":[OSD([sQuery(id+"F63.wireOp",EDGE,"E100"),sQuery(id+"F63.wireOp",EDGE,"E101")])],"isStart":true});
            cPlane(context, id + "F65", {"entities" : qUnion([Q0, Q1, Q2]), "cplaneType" : CPlaneType.THREE_POINT, "offset" : 152.4 * mm, "width" : 152.4 * mm, "height" : 152.4 * mm});
        }
        {
            var Q0;
            Q0=qCreatedBy(id+"F65.planeOp",FACE);
            var sketch = newSketch(context, id + "F66", { "sketchPlane" : qUnion([Q0])});
            skPoint(sketch, "E102.1", {"position": v(1355.72, 20.34) * mm});
            skPoint(sketch, "E102.2", {"position": v(932.24, 22.79) * mm});
            skPoint(sketch, "E102.3", {"position": v(1037.8, 94.45) * mm});
            skLineSegment(sketch, "E103", {"start": v(932.24, 22.79) * mm, "end": v(1037.8, 94.45) * mm});
            skLineSegment(sketch, "E104", {"start": v(1037.8, 94.45) * mm, "end": v(1355.72, 20.34) * mm});
            skLineSegment(sketch, "E105", {"start": v(1355.72, 20.34) * mm, "end": v(932.24, 22.79) * mm});
            skSolve(sketch);
        }
        {
            var Q0;
            Q0 = qSketchRegion(id + "F66", true);
            extrude(context, id + "F67", {"entities" : qUnion([Q0]), "depth" : 3.17 * mm});
        }
        {
            var Q0;
            Q0=makeQuery(id+"F67.opExtrude","SWEPT_BODY",BODY,{"disambiguationData":[OSD([sQuery(id+"F66.wireOp",EDGE,"E103"),sQuery(id+"F66.wireOp",EDGE,"E104"),sQuery(id+"F66.wireOp",EDGE,"E105")])]});
            var Q1;
            Q1=makeQuery(id+"F61.opExtrude","SWEPT_BODY",BODY,{"disambiguationData":[OSD([sQuery(id+"F60.wireOp",EDGE,"E94"),sQuery(id+"F60.wireOp",EDGE,"E95"),sQuery(id+"F60.wireOp",EDGE,"E96")])]});
            var Q2;
            Q2=qCreatedBy(makeId("Right.planeOp"),FACE);
            mirror(context, id + "F68", {"entities" : qUnion([Q0, Q1]), "mirrorPlane" : qUnion([Q2])});
        }
        {
            var Q0;
            Q0=makeQuery(id+"F54.opExtrude","CAP_EDGE",EDGE,{"disambiguationData":[OSD([sQuery(id+"F53.wireOp",EDGE,"E89.2")])],"isStart":true});
            cPlane(context, id + "F69", {"entities" : qUnion([Q0]), "cplaneType" : CPlaneType.LINE_ANGLE, "offset" : 152.4 * mm, "angle" : 45 * degree, "width" : 152.4 * mm, "height" : 152.4 * mm});
        }
        {
            var Q0;
            Q0=qCreatedBy(id+"F69.planeOp",FACE);
            var sketch = newSketch(context, id + "F70", { "sketchPlane" : qUnion([Q0])});
            skPoint(sketch, "E106.1", {"position": v(95.8, 535.6) * mm});
            skPoint(sketch, "E107.0", {"position": v(318.99, 451.57) * mm});
            skLineSegment(sketch, "E108", {"start": v(318.99, 451.57) * mm, "end": v(95.8, 535.6) * mm});
            skLineSegment(sketch, "E109", {"start": v(318.99, 451.57) * mm, "end": v(307.05, 488.92) * mm});
            skLineSegment(sketch, "E110", {"start": v(307.05, 488.92) * mm, "end": v(95.8, 622.6) * mm});
            skLineSegment(sketch, "E111", {"start": v(95.8, 622.6) * mm, "end": v(95.8, 535.6) * mm});
            skSolve(sketch);
        }
        {
            var Q0;
            Q0 = qSketchRegion(id + "F70", true);
            extrude(context, id + "F71", {"entities" : qUnion([Q0]), "depth" : 3.17 * mm});
        }
        {
            var Q0;
            Q0=makeQuery(id+"F48.opExtrude","CAP_EDGE",EDGE,{"disambiguationData":[OSD([sQuery(id+"F47.wireOp",EDGE,"E80")])],"isStart":true});
            cPlane(context, id + "F72", {"entities" : qUnion([Q0]), "cplaneType" : CPlaneType.LINE_ANGLE, "offset" : 152.4 * mm, "angle" : 51.5 * degree, "width" : 152.4 * mm, "height" : 152.4 * mm});
        }
        {
            var Q0;
            Q0=qCreatedBy(id+"F72.planeOp",FACE);
            var sketch = newSketch(context, id + "F73", { "sketchPlane" : qUnion([Q0])});
            skLineSegment(sketch, "E112.0", {"start": v(316.32, 536.71) * mm, "end": v(278.86, 536.71) * mm});
            skLineSegment(sketch, "E113.0", {"start": v(316.32, 621.8) * mm, "end": v(316.32, 536.71) * mm});
            skLineSegment(sketch, "E114", {"start": v(316.32, 621.8) * mm, "end": v(264.25, 621.8) * mm});
            skLineSegment(sketch, "E115", {"start": v(264.25, 621.8) * mm, "end": v(278.86, 536.71) * mm});
            skPoint(sketch, "E116.orphan", {"position": v(316.32, 534.8) * mm});
            skPoint(sketch, "E117.orphan", {"position": v(317.5, 536.71) * mm});
            skSolve(sketch);
        }
        {
            var Q0;
            Q0 = qSketchRegion(id + "F73", true);
            extrude(context, id + "F74", {"entities" : qUnion([Q0]), "oppositeDirection" : true, "depth" : 3.17 * mm});
        }
        {
            var Q0;
            Q0=makeQuery(id+"F71.opExtrude","SWEPT_BODY",BODY,{"disambiguationData":[OSD([sQuery(id+"F70.wireOp",EDGE,"E108"),sQuery(id+"F70.wireOp",EDGE,"E109"),sQuery(id+"F70.wireOp",EDGE,"E110"),sQuery(id+"F70.wireOp",EDGE,"E111")])]});
            var Q1;
            Q1=makeQuery(id+"F74.opExtrude","SWEPT_BODY",BODY,{"disambiguationData":[OSD([sQuery(id+"F73.wireOp",EDGE,"E112.0"),sQuery(id+"F73.wireOp",EDGE,"E113.0"),sQuery(id+"F73.wireOp",EDGE,"E114"),sQuery(id+"F73.wireOp",EDGE,"E115")])]});
            var Q2;
            Q2=qCreatedBy(makeId("Right.planeOp"),FACE);
            mirror(context, id + "F75", {"entities" : qUnion([Q0, Q1]), "mirrorPlane" : qUnion([Q2])});
        }
    });
